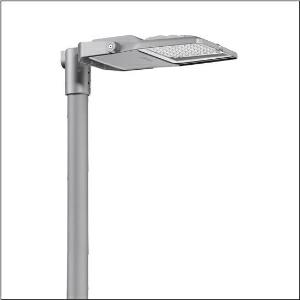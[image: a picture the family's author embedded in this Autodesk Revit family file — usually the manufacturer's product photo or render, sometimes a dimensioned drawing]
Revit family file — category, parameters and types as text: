
# Revit family: floodlight_fl_21_mini___pl52_5xa7775d2d3a_ca02
name_source: partatom
category: Lighting Fixtures
units: mm (PartAtom-declared; Revit-internal decimal feet)

## family parameters
Cut with Voids When Loaded = No
Host = Face
Light Source = No
Part Type = Normal
Room Calculation Point = No
Round Connector Dimension = Use Diameter
Shared = No

## types (1)
- --- (1 x LED, 17840 lm, 142.9 W, 3000K)
    Apparent Load = 143 VA
    CIE Flux Codes = 26 60 98 100 100
    Color Rendering = 70
    Color Temperature = 3000K
    Default Elevation = 1800 mm
    Description = Floodlight FL 21 mini, floodlight, primary light control with lens, of PMMA, primary optical cover: protective disc, of toughened safety glass, transparent, light distribution: PL52, light emission: direct distribution, installation type: surface-mounted, LED, High Power LED, rated luminous flux: 17.840lm, luminous efficacy: 125lm/W, light colour: 730, colour temperature: 3000K, control: flexible luminous flux parameterisation, time-dependent luminous flux control, constant luminous flux control, overheat protection, presetting dimming logarithmic, with terminal, 6-pole, mains connection: 220..240V, AC, 50/60Hz, start of lifetime: 143W, end of service life: 151W, reduction: 63W, luminaire housing, of diecast aluminium, powder-coated, Siteco® metallic grey (DB 702S), corrosivity category C5 mid according to DIN EN ISO 12944, sealing non-destructively replaceable, please order mast flange separately, mast bracket, of steel, galvanised, powder-coated, Siteco® metallic grey (DB 702S), Smart Interface above, protection rating (complete): IP66, insulation class (complete): insulation class II (safety insulation), certification: CE, ENEC, VDE, protection symbol: D, impact resistance: IK08, permissible operating ambient temperature: -40..+40°C, permissible operating ambient temperature for outdoor applications: -40..+50°C, standard: DIN EN 12944, LABS conformity tested according to VDMA 24364:2018-05, packaging unit: 1 piece

Light Distribution: PL52
    Height = 70 mm
    Lamp = 1 x LED
    Lamp Light Flux = 17840 lm
    Lamp Power = 142.9 W
    Lamp count = 1
    Length = 485 mm
    Luminous efficacy = 125 lm/W
    Manufacturer = Siteco
    ModVariant = No
    Model = 5XA7775D2D3A
    Number of Poles = 1
    OnlyDefault = Yes
    Power Factor = 1
    Product Name = Floodlight FL 21 mini | PL52
    Product group = floodlight | pylon annexe
    ProductGroupID = 6200
    Protection Class = Protection class II
    Protection Degree = IP 66
    RLX_Detail_Level = 1
    RLX_Emergency_Light_Flux = 0 lm
    RLX_Emergency_Type = 0
    RLX_Emergency_Type_DB = No
    RlxData = <blob elided: 101393 chars, md5=23d16551>
    Socket = socket
    Standby Power = 0 W
    System Light Flux = 17840 lm
    System Power = 143 W
    Type Comments = factory setting: luminous flux: 100 % | dim-lin: 254 | 730 mA
    Type Image = l_1007125.jpg
    URL = http://relux.com
    VarID = @adj_113337
    Voltage = 0 V
    Weight = 0.00 kg
    Width = 337 mm

## geometry (parser evidence)
native form markers: Blend x4, Sweep x11
no freeform markers — native parametric forms only
